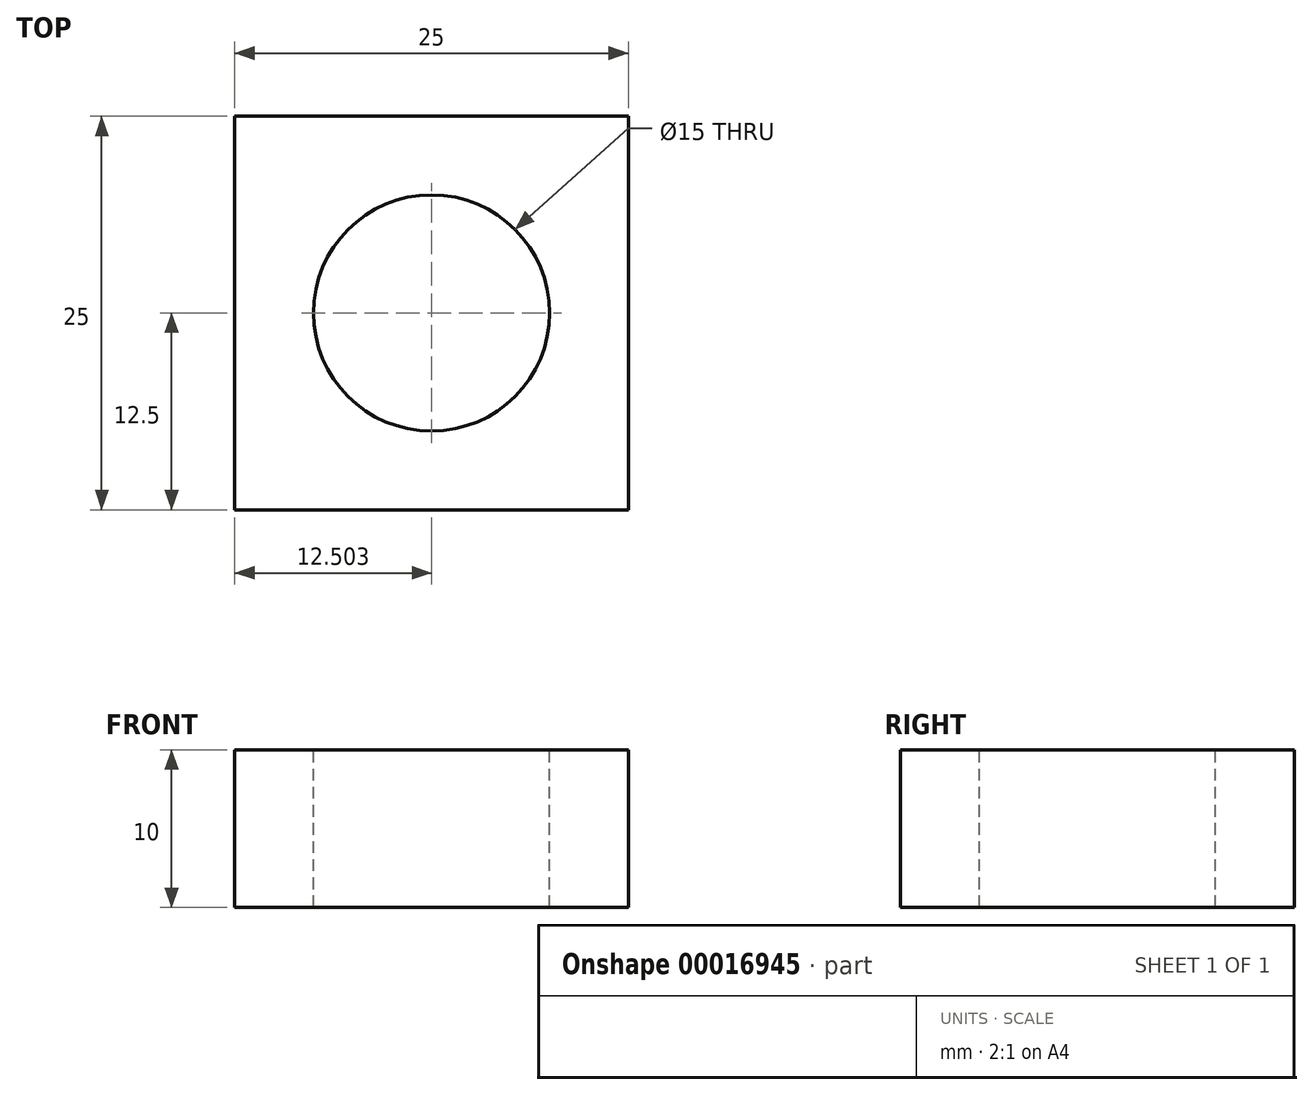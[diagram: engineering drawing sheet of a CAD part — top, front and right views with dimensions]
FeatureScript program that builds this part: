
annotation { "Feature Type Name" : "Feature", "Feature Type Description" : "" }
export const myFeature = defineFeature(function(context is Context, id is Id, definition is map)
    precondition{}
    {
        {
            var Q0;
            Q0=qCreatedBy(makeId("Front.planeOp"),FACE);
            var sketch = newSketch(context, id + "F0", { "sketchPlane" : qUnion([Q0])});
            skLineSegment(sketch, "E0.bottom", {"start": v(-20.9, 1.82) * mm, "end": v(4.1, 1.82) * mm});
            skLineSegment(sketch, "E0.top", {"start": v(-20.9, -8.18) * mm, "end": v(4.1, -8.18) * mm});
            skLineSegment(sketch, "E0.left", {"start": v(-20.9, 1.82) * mm, "end": v(-20.9, -8.18) * mm});
            skLineSegment(sketch, "E0.right", {"start": v(4.1, 1.82) * mm, "end": v(4.1, -8.18) * mm});
            skSolve(sketch);
        }
        {
            var Q0;
            Q0=makeQuery(id+"F0.imprint","IMPRINT",FACE,{"disambiguationData":[TD([[makeQuery(id+"F0.imprint","IMPRINT",EDGE,{"derivedFrom":sQuery(id+"F0.wireOp",EDGE,"E0.bottom")}),-1.0]])]});
            extrude(context, id + "F1", {"entities" : qUnion([Q0]), "depth" : 25 * mm});
        }
        {
            var Q0;
            Q0=makeQuery(id+"F1.opExtrude","SWEPT_FACE",FACE,{"disambiguationData":[OSD([sQuery(id+"F0.wireOp",EDGE,"E0.bottom")])]});
            var sketch = newSketch(context, id + "F2", { "sketchPlane" : qUnion([Q0])});
            skCircle(sketch, "E1", {"center": v(-8.4, -12.5) * mm, "radius": 7.5 * mm});
            skSolve(sketch);
        }
        {
            var Q0;
            Q0=makeQuery(id+"F2.imprint","IMPRINT",FACE,{"disambiguationData":[TD([[makeQuery(id+"F2.imprint","IMPRINT",EDGE,{"derivedFrom":sQuery(id+"F2.wireOp",EDGE,"E1")}),1.0]])]});
            extrude(context, id + "F3", {"entities" : qUnion([Q0]), "operationType" : NewBodyOperationType.REMOVE, "endBound" : BoundingType.THROUGH_ALL, "oppositeDirection" : true, "depth" : 25 * mm});
        }
    });
